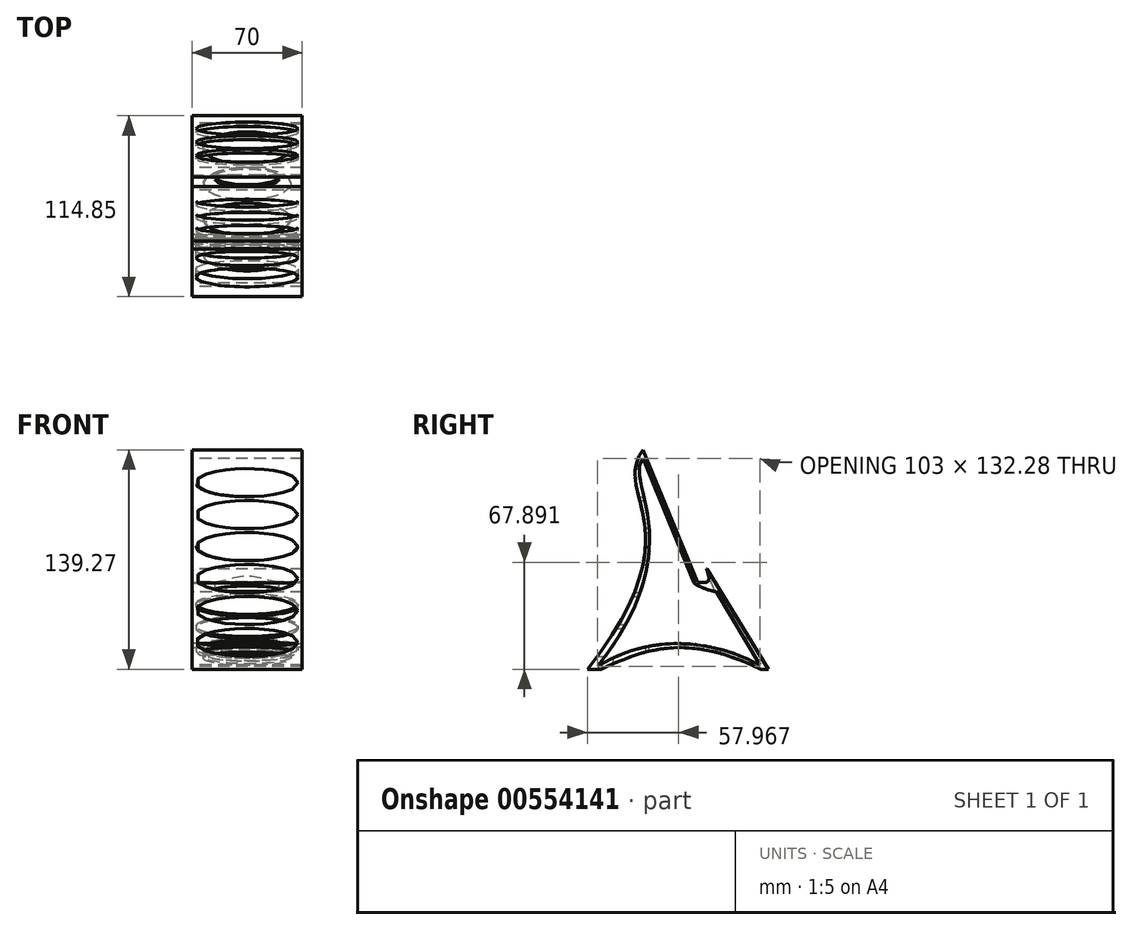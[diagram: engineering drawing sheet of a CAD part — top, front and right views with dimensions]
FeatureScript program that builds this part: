
annotation { "Feature Type Name" : "Feature", "Feature Type Description" : "" }
export const myFeature = defineFeature(function(context is Context, id is Id, definition is map)
    precondition{}
    {
        {
            var Q0;
            Q0=qCreatedBy(makeId("Right.planeOp"),FACE);
            var sketch = newSketch(context, id + "F0", { "sketchPlane" : qUnion([Q0])});
            skFitSpline(sketch, "E0", {"points": [v(-65.05, 0) * mm, v(-29.92, 139.27) * mm], "startDerivative": vector(210.97, 269.62) * mm, "endDerivative": vector(62.07, 87.75) * mm});
            skFitSpline(sketch, "E1", {"points": [v(-56.41, 0) * mm, v(45.2, 0) * mm], "startDerivative": vector(85.43, 39.38) * mm, "endDerivative": vector(140.76, -68.45) * mm});
            skFitSpline(sketch, "E2", {"points": [v(49.8, 0) * mm, v(10.74, 63.83) * mm], "startDerivative": vector(-39.06, 63.83) * mm, "endDerivative": vector(-39.06, 63.83) * mm});
            skLineSegment(sketch, "E3", {"start": v(-29.92, 139.27) * mm, "end": v(4.83, 55.39) * mm});
            skFitSpline(sketch, "E4", {"points": [v(-58.58, 1.75) * mm, v(-29.9, 134.03) * mm], "startDerivative": vector(181.66, 231.88) * mm, "endDerivative": vector(35.66, 50.36) * mm});
            skFitSpline(sketch, "E5", {"points": [v(-58.58, 1.75) * mm, v(44.42, 2.6) * mm], "startDerivative": vector(96.07, 60.59) * mm, "endDerivative": vector(95.42, -52.13) * mm});
            skFitSpline(sketch, "E6", {"points": [v(4.83, 55.39) * mm, v(10.74, 63.83) * mm], "startDerivative": vector(36.77, -7.47) * mm, "endDerivative": vector(2.44, 4) * mm});
            skLineSegment(sketch, "E7", {"start": v(-65.05, 0) * mm, "end": v(-56.41, 0) * mm});
            skLineSegment(sketch, "E8", {"start": v(45.2, 0) * mm, "end": v(49.8, 0) * mm});
            skLineSegment(sketch, "E9", {"start": v(16.98, 49.19) * mm, "end": v(44.42, 2.6) * mm});
            skLineSegment(sketch, "E10", {"start": v(-29.9, 134.03) * mm, "end": v(2.49, 54.83) * mm});
            skFitSpline(sketch, "E11", {"points": [v(2.49, 54.83) * mm, v(16.98, 49.19) * mm], "startDerivative": vector(13.4, -9.27) * mm, "endDerivative": vector(11.5, -1.96) * mm});
            skSolve(sketch);
        }
        {
            var Q0;
            Q0=makeQuery(id+"F0.imprint","IMPRINT",FACE,{"disambiguationData":[TD([[makeQuery(id+"F0.imprint","IMPRINT",EDGE,{"derivedFrom":sQuery(id+"F0.wireOp",EDGE,"E0")}),-1.0]])]});
            extrude(context, id + "F1", {"entities" : qUnion([Q0]), "depth" : 70 * mm});
        }
        {
            var Q0;
            Q0=makeQuery(id+"F1.opExtrude","SWEPT_FACE",FACE,{"disambiguationData":[OSD([sQuery(id+"F0.wireOp",EDGE,"E9")])]});
            var sketch = newSketch(context, id + "F2", { "sketchPlane" : qUnion([Q0])});
            skEllipse(sketch, "E12", {"center": v(35, 23.43) * mm, "majorRadius": 32.5 * mm, "minorRadius": 7.82 * mm, "majorAxis": v(1, 0)});
            skEllipse(sketch, "E13.0.1.0", {"center": v(35, 6.93) * mm, "majorRadius": 32.5 * mm, "minorRadius": 7.82 * mm, "majorAxis": v(1, 0)});
            skEllipse(sketch, "E13.0.2.0", {"center": v(35, -9.57) * mm, "majorRadius": 32.5 * mm, "minorRadius": 7.82 * mm, "majorAxis": v(1, 0)});
            skLineSegment(sketch, "E13.direction1", {"start": v(35, 23.43) * mm, "end": v(57.03, 23.43) * mm, "construction": true});
            skLineSegment(sketch, "E13.direction2", {"start": v(35, 23.43) * mm, "end": v(35, 6.93) * mm, "construction": true});
            skSolve(sketch);
        }
        {
            var Q0;
            Q0=qSketchRegion(id+"F2",true);
            var Q1;
            Q1=makeQuery(id+"F1.opExtrude","SWEPT_FACE",FACE,{"disambiguationData":[OSD([sQuery(id+"F0.wireOp",EDGE,"E2")])]});
            extrude(context, id + "F3", {"entities" : qUnion([Q0]), "operationType" : NewBodyOperationType.REMOVE, "endBound" : BoundingType.UP_TO_SURFACE, "oppositeDirection" : true, "endBoundEntityFace" : qUnion([Q1]), "depth" : 25 * mm});
        }
        {
            var Q0;
            Q0=qCreatedBy(makeId("Top.planeOp"),FACE);
            var sketch = newSketch(context, id + "F4", { "sketchPlane" : qUnion([Q0])});
            skEllipse(sketch, "E14", {"center": v(35, -38.54) * mm, "majorRadius": 27.85 * mm, "minorRadius": 10.2 * mm, "majorAxis": v(1, 0)});
            skEllipse(sketch, "E15.0.1.0", {"center": v(35, -15.94) * mm, "majorRadius": 27.85 * mm, "minorRadius": 10.2 * mm, "majorAxis": v(1, 0)});
            skEllipse(sketch, "E15.0.2.0", {"center": v(35, 6.66) * mm, "majorRadius": 27.85 * mm, "minorRadius": 10.2 * mm, "majorAxis": v(1, 0)});
            skEllipse(sketch, "E15.0.3.0", {"center": v(35, 29.26) * mm, "majorRadius": 27.85 * mm, "minorRadius": 10.2 * mm, "majorAxis": v(1, 0)});
            skLineSegment(sketch, "E15.direction1", {"start": v(35, -38.54) * mm, "end": v(60, -38.54) * mm, "construction": true});
            skLineSegment(sketch, "E15.direction2", {"start": v(35, -38.54) * mm, "end": v(35, -15.94) * mm, "construction": true});
            skSolve(sketch);
        }
        {
            var Q0;
            Q0=qSketchRegion(id+"F4",true);
            var Q1;
            Q1=makeQuery(id+"F1.opExtrude","SWEPT_FACE",FACE,{"disambiguationData":[OSD([sQuery(id+"F0.wireOp",EDGE,"E5")])]});
            extrude(context, id + "F5", {"entities" : qUnion([Q0]), "operationType" : NewBodyOperationType.REMOVE, "endBound" : BoundingType.UP_TO_SURFACE, "endBoundEntityFace" : qUnion([Q1]), "depth" : 25 * mm});
        }
        {
            var Q0;
            Q0=qCreatedBy(makeId("Front.planeOp"),FACE);
            cPlane(context, id + "F6", {"entities" : qUnion([Q0]), "cplaneType" : CPlaneType.OFFSET, "offset" : 70 * mm, "width" : 150 * mm, "height" : 150 * mm});
        }
        {
            var Q0;
            Q0=qCreatedBy(id+"F6.planeOp",FACE);
            var sketch = newSketch(context, id + "F7", { "sketchPlane" : qUnion([Q0])});
            skEllipse(sketch, "E16", {"center": v(35, 118.52) * mm, "majorRadius": 32.5 * mm, "minorRadius": 8.93 * mm, "majorAxis": v(1, 0)});
            skEllipse(sketch, "E17.0.1.0", {"center": v(35, 98.22) * mm, "majorRadius": 32.5 * mm, "minorRadius": 8.93 * mm, "majorAxis": v(1, 0)});
            skEllipse(sketch, "E17.0.2.0", {"center": v(35, 77.92) * mm, "majorRadius": 32.5 * mm, "minorRadius": 8.93 * mm, "majorAxis": v(1, 0)});
            skEllipse(sketch, "E17.0.3.0", {"center": v(35, 57.62) * mm, "majorRadius": 32.5 * mm, "minorRadius": 8.93 * mm, "majorAxis": v(1, 0)});
            skEllipse(sketch, "E17.0.4.0", {"center": v(35, 37.32) * mm, "majorRadius": 32.5 * mm, "minorRadius": 8.93 * mm, "majorAxis": v(1, 0)});
            skEllipse(sketch, "E17.0.5.0", {"center": v(35, 17.02) * mm, "majorRadius": 32.5 * mm, "minorRadius": 8.93 * mm, "majorAxis": v(1, 0)});
            skLineSegment(sketch, "E17.direction1", {"start": v(35, 118.52) * mm, "end": v(60, 118.52) * mm, "construction": true});
            skLineSegment(sketch, "E17.direction2", {"start": v(35, 118.52) * mm, "end": v(35, 98.22) * mm, "construction": true});
            skSolve(sketch);
        }
        {
            var Q0;
            Q0=makeQuery(id+"F7.imprint","IMPRINT",FACE,{"disambiguationData":[TD([[makeQuery(id+"F7.imprint","IMPRINT",EDGE,{"derivedFrom":sQuery(id+"F7.wireOp",EDGE,"E17.0.3.0")}),1.0]])]});
            var Q1;
            Q1=makeQuery(id+"F7.imprint","IMPRINT",FACE,{"disambiguationData":[TD([[makeQuery(id+"F7.imprint","IMPRINT",EDGE,{"derivedFrom":sQuery(id+"F7.wireOp",EDGE,"E17.0.4.0")}),1.0]])]});
            var Q2;
            Q2=makeQuery(id+"F7.imprint","IMPRINT",FACE,{"disambiguationData":[TD([[makeQuery(id+"F7.imprint","IMPRINT",EDGE,{"derivedFrom":sQuery(id+"F7.wireOp",EDGE,"E17.0.5.0")}),1.0]])]});
            var Q3;
            Q3=makeQuery(id+"F1.opExtrude","SWEPT_FACE",FACE,{"disambiguationData":[OSD([sQuery(id+"F0.wireOp",EDGE,"E4")])]});
            extrude(context, id + "F8", {"entities" : qUnion([Q0, Q1, Q2]), "operationType" : NewBodyOperationType.REMOVE, "endBound" : BoundingType.UP_TO_SURFACE, "oppositeDirection" : true, "endBoundEntityFace" : qUnion([Q3]), "depth" : 25 * mm});
        }
        {
            var Q0;
            Q0=makeQuery(id+"F7.imprint","IMPRINT",FACE,{"disambiguationData":[TD([[makeQuery(id+"F7.imprint","IMPRINT",EDGE,{"derivedFrom":sQuery(id+"F7.wireOp",EDGE,"E16")}),1.0]])]});
            var Q1;
            Q1=makeQuery(id+"F7.imprint","IMPRINT",FACE,{"disambiguationData":[TD([[makeQuery(id+"F7.imprint","IMPRINT",EDGE,{"derivedFrom":sQuery(id+"F7.wireOp",EDGE,"E17.0.1.0")}),1.0]])]});
            var Q2;
            Q2=makeQuery(id+"F7.imprint","IMPRINT",FACE,{"disambiguationData":[TD([[makeQuery(id+"F7.imprint","IMPRINT",EDGE,{"derivedFrom":sQuery(id+"F7.wireOp",EDGE,"E17.0.2.0")}),1.0]])]});
            var Q3;
            Q3=makeQuery(id+"F1.opExtrude","SWEPT_FACE",FACE,{"disambiguationData":[OSD([sQuery(id+"F0.wireOp",EDGE,"E3")])]});
            extrude(context, id + "F9", {"entities" : qUnion([Q0, Q1, Q2]), "operationType" : NewBodyOperationType.REMOVE, "endBound" : BoundingType.UP_TO_SURFACE, "oppositeDirection" : true, "endBoundEntityFace" : qUnion([Q3]), "depth" : 25 * mm});
        }
        {
            var Q0;
            Q0=makeQuery(id+"F1.opExtrude","SWEPT_FACE",FACE,{"disambiguationData":[OSD([sQuery(id+"F0.wireOp",EDGE,"E3")])]});
            var Q1;
            Q1=makeQuery(id+"F1.opExtrude","SWEPT_EDGE",EDGE,{"disambiguationData":[OSD([sQuery(id+"F0.wireOp",EDGE,"E0"),sQuery(id+"F0.wireOp",EDGE,"E3")])]});
            cPlane(context, id + "F10", {"entities" : qUnion([Q0, Q1]), "cplaneType" : CPlaneType.LINE_ANGLE, "offset" : 25 * mm, "angle" : 90 * degree, "width" : 150 * mm, "height" : 150 * mm});
        }
        {
            var Q0;
            Q0=qCreatedBy(id+"F10.planeOp",FACE);
            var sketch = newSketch(context, id + "F11", { "sketchPlane" : qUnion([Q0])});
            skEllipse(sketch, "E18", {"center": v(35, 29.66) * mm, "majorRadius": 20.28 * mm, "minorRadius": 4 * mm, "majorAxis": v(-1, 0)});
            skSolve(sketch);
        }
        {
            var Q0;
            Q0=qSketchRegion(id+"F11",true);
            var Q1;
            Q1=makeQuery(id+"F1.opExtrude","SWEPT_FACE",FACE,{"disambiguationData":[OSD([sQuery(id+"F0.wireOp",EDGE,"E11")])]});
            extrude(context, id + "F12", {"entities" : qUnion([Q0]), "operationType" : NewBodyOperationType.REMOVE, "endBound" : BoundingType.UP_TO_SURFACE, "oppositeDirection" : true, "endBoundEntityFace" : qUnion([Q1]), "depth" : 25 * mm});
        }
    });
